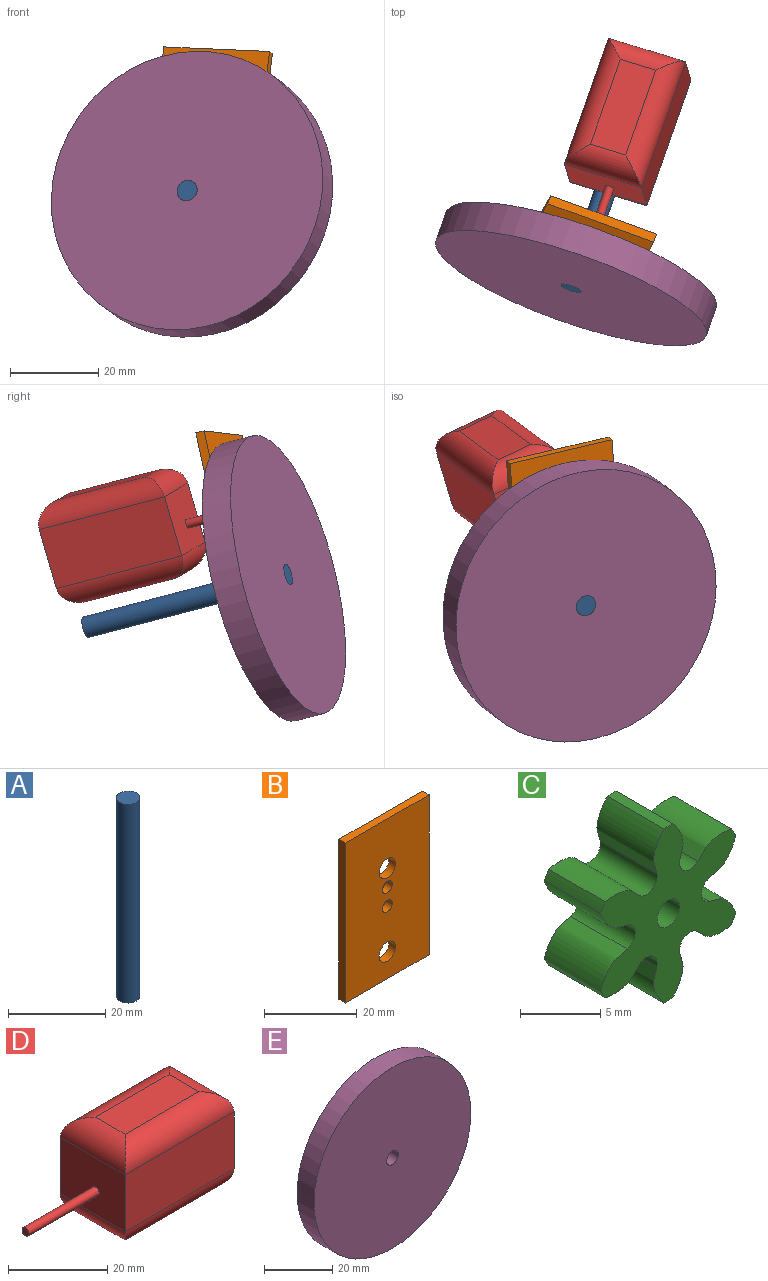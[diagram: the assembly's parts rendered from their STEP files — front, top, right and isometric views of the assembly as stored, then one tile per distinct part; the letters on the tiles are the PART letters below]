
ASSEMBLY  parts=5 mates=4
PART A: 3 faces, bbox 4.8x4.8x50 mm
  f0: cylinder r=2.4mm len=50mm, axis (0,0,-1), area 754mm2, adj f1,f2
  f1: plane 4.8x4.8mm, normal (0,0,1), area 18.1mm2, adj f0
  f2: plane 4.8x4.8mm, normal (0,0,-1), area 18.1mm2, adj f0
PART B: 10 faces, bbox 25.5x2x42.2 mm
  f0: plane 25.5x2mm, normal (0,0,1), area 51mm2, adj f1,f7,f8,f9
  f1: plane 42.2x2mm, normal (-1,0,0), area 84.4mm2, adj f0,f2,f8,f9
  f2: plane 25.5x2mm, normal (0,0,-1), area 51mm2, adj f1,f7,f8,f9
  f3: cylinder r=2.5mm len=5mm, axis (0,1,0), area 31.4mm2, adj f8,f9
  f4: cylinder r=1.5mm len=3mm, axis (0,1,0), area 18.8mm2, adj f8,f9
  f5: cylinder r=1.5mm len=3mm, axis (0,1,0), area 18.8mm2, adj f8,f9
  f6: cylinder r=2.5mm len=5mm, axis (0,1,0), area 31.4mm2, adj f8,f9
  f7: plane 42.2x2mm, normal (1,0,0), area 84.4mm2, adj f0,f2,f8,f9
  f8: plane 42.2x25.5mm, normal (0,-1,0), area 1022.7mm2, adj f0,f1,f2,f3,f4,f5,f6,f7
  f9: plane 42.2x25.5mm, normal (0,1,0), area 1022.7mm2, adj f0,f1,f2,f3,f4,f5,f6,f7
PART C: 27 faces, bbox 12x5x13.4 mm
  f0: cylinder r=6.67mm len=5mm, axis (0,1,0), area 3.9mm2, adj f5,f6,f18,f25
  f1: cylinder r=6.67mm len=5mm, axis (0,1,0), area 3.9mm2, adj f5,f6,f22,f24
  f2: cylinder r=6.67mm len=5mm, axis (0,1,0), area 3.9mm2, adj f5,f6,f15,f19
  f3: cylinder r=6.67mm len=5mm, axis (0,1,0), area 3.9mm2, adj f5,f6,f9,f16
  f4: cylinder r=6.67mm len=5mm, axis (0,1,0), area 3.9mm2, adj f5,f6,f13,f21
  f5: plane 13.39x11.99mm, normal (0,-1,0), area 71.7mm2, adj f0,f1,f2,f3,f4,f7,f8,f9
  f6: plane 13.39x11.99mm, normal (0,1,0), area 71.7mm2, adj f0,f1,f2,f3,f4,f7,f8,f9
  f7: cylinder r=1mm len=5mm, axis (0,1,0), area 31.4mm2, adj f5,f6
  f8: cylinder r=6.67mm len=5mm, axis (0,1,0), area 3.9mm2, adj f5,f6,f10,f12
  f9: extruded ~5x2.33mm, area 16.8mm2, adj f3,f5,f6,f11
  f10: extruded ~5x2.33mm, area 16.8mm2, adj f5,f6,f8,f11
  f11: cylinder r=0.94mm len=5mm, axis (0,1,0), area 12.5mm2, adj f5,f6,f9,f10
  f12: extruded ~5x2.96mm, area 16.8mm2, adj f5,f6,f8,f14
  f13: extruded ~5x3.06mm, area 16.8mm2, adj f4,f5,f6,f14
  f14: cylinder r=0.94mm len=5mm, axis (0,1,0), area 12.5mm2, adj f5,f6,f12,f13
  f15: extruded ~5x3.06mm, area 16.8mm2, adj f2,f5,f6,f17
  f16: extruded ~5x2.96mm, area 16.8mm2, adj f3,f5,f6,f17
  f17: cylinder r=0.94mm len=5mm, axis (0,1,0), area 12.5mm2, adj f5,f6,f15,f16
  f18: extruded ~5x2.96mm, area 16.8mm2, adj f0,f5,f6,f20
  f19: extruded ~5x3.06mm, area 16.8mm2, adj f2,f5,f6,f20
  f20: cylinder r=0.94mm len=5mm, axis (0,1,0), area 12.5mm2, adj f5,f6,f18,f19
  f21: extruded ~5x3.06mm, area 16.8mm2, adj f4,f5,f6,f23
  f22: extruded ~5x2.96mm, area 16.8mm2, adj f1,f5,f6,f23
  f23: cylinder r=0.94mm len=5mm, axis (0,1,0), area 12.5mm2, adj f5,f6,f21,f22
  f24: extruded ~5x2.33mm, area 16.8mm2, adj f1,f5,f6,f26
  f25: extruded ~5x2.33mm, area 16.8mm2, adj f0,f5,f6,f26
  f26: cylinder r=0.94mm len=5mm, axis (0,1,0), area 12.5mm2, adj f5,f6,f24,f25
PART D: 16 faces, bbox 51x18.5x24 mm
  f0: plane 18.5x14mm, normal (-1,0,0), area 255.9mm2, adj f4,f5,f9,f10,f14
  f1: plane 21x8.5mm, normal (0,0,-1), area 178.5mm2, adj f6,f7,f8,f9
  f2: plane 18.5x14mm, normal (1,0,0), area 259mm2, adj f4,f5,f6,f13
  f3: plane 21x8.5mm, normal (0,0,1), area 178.5mm2, adj f10,f11,f12,f13
  f4: plane 31x14mm, normal (0,-1,0), area 434mm2, adj f0,f2,f7,f11
  f5: plane 31x14mm, normal (0,1,0), area 434mm2, adj f0,f2,f8,f12
  f6: cylinder r=5mm len=18.5mm, axis (0,1,0), area 116.8mm2, adj f1,f2,f7,f8
  f7: cylinder r=5mm len=31mm, axis (-1,0,0), area 214.9mm2, adj f1,f4,f6,f9
  f8: cylinder r=5mm len=31mm, axis (1,0,0), area 214.9mm2, adj f1,f5,f6,f9
  f9: cylinder r=5mm len=18.5mm, axis (0,-1,0), area 116.8mm2, adj f0,f1,f7,f8
  f10: cylinder r=5mm len=18.5mm, axis (0,1,0), area 116.8mm2, adj f0,f3,f11,f12
  f11: cylinder r=5mm len=31mm, axis (1,0,0), area 214.9mm2, adj f3,f4,f10,f13
  f12: cylinder r=5mm len=31mm, axis (-1,0,0), area 214.9mm2, adj f3,f5,f10,f13
  f13: cylinder r=5mm len=18.5mm, axis (0,-1,0), area 116.8mm2, adj f2,f3,f11,f12
  f14: cylinder r=1mm len=20mm, axis (1,0,0), area 125.7mm2, adj f0,f15
  f15: plane 2x2mm, normal (-1,0,0), area 3.1mm2, adj f14
PART E: 119 faces, bbox 65x7x65 mm
  f0: cylinder r=2.4mm len=7mm, axis (0,1,0), area 105.6mm2, adj f2,f118
  f1: cylinder r=32.5mm len=65mm, axis (0,1,0), area 1429.4mm2, adj f2,f3
  f2: plane 65x65mm, normal (0,-1,0), area 3300.2mm2, adj f0,f1
  f3: plane 65x65mm, normal (0,1,0), area 1623.9mm2, adj f1,f4,f5,f6,f7,f8,f9,f10
  f4: cylinder r=25mm len=5mm, axis (0,1,0), area 6.1mm2, adj f3,f31,f33,f115
  f5: cylinder r=25mm len=5mm, axis (0,1,0), area 6.1mm2, adj f3,f31,f112,f114
  f6: cylinder r=25mm len=5mm, axis (0,1,0), area 6.1mm2, adj f3,f31,f105,f109
  f7: cylinder r=25mm len=5mm, axis (0,1,0), area 6.1mm2, adj f3,f31,f106,f111
  f8: cylinder r=25mm len=5mm, axis (0,1,0), area 6.1mm2, adj f3,f31,f103,f108
  f9: cylinder r=25mm len=5mm, axis (0,1,0), area 6.1mm2, adj f3,f31,f100,f102
  f10: cylinder r=25mm len=5mm, axis (0,1,0), area 6.1mm2, adj f3,f31,f97,f99
  f11: cylinder r=25mm len=5mm, axis (0,1,0), area 6.1mm2, adj f3,f31,f94,f96
  f12: cylinder r=25mm len=5mm, axis (0,1,0), area 6.1mm2, adj f3,f31,f87,f91
  f13: cylinder r=25mm len=5mm, axis (0,1,0), area 6.1mm2, adj f3,f31,f84,f88
  f14: cylinder r=25mm len=5mm, axis (0,1,0), area 6.1mm2, adj f3,f31,f81,f85
  f15: cylinder r=25mm len=5mm, axis (0,1,0), area 6.1mm2, adj f3,f31,f82,f93
  f16: cylinder r=25mm len=5mm, axis (0,1,0), area 6.1mm2, adj f3,f31,f79,f90
  f17: cylinder r=25mm len=5mm, axis (0,1,0), area 6.1mm2, adj f3,f31,f76,f78
  f18: cylinder r=25mm len=5mm, axis (0,1,0), area 6.1mm2, adj f3,f31,f73,f75
  f19: cylinder r=25mm len=5mm, axis (0,1,0), area 6.1mm2, adj f3,f31,f70,f72
  f20: cylinder r=25mm len=5mm, axis (0,1,0), area 6.1mm2, adj f3,f31,f63,f67
  f21: cylinder r=25mm len=5mm, axis (0,1,0), area 6.1mm2, adj f3,f31,f60,f64
  f22: cylinder r=25mm len=5mm, axis (0,1,0), area 6.1mm2, adj f3,f31,f57,f61
  f23: cylinder r=25mm len=5mm, axis (0,1,0), area 6.1mm2, adj f3,f31,f54,f58
  f24: cylinder r=25mm len=5mm, axis (0,1,0), area 6.1mm2, adj f3,f31,f51,f55
  f25: cylinder r=25mm len=5mm, axis (0,1,0), area 6.1mm2, adj f3,f31,f48,f52
  f26: cylinder r=25mm len=5mm, axis (0,1,0), area 6.1mm2, adj f3,f31,f45,f49
  f27: cylinder r=25mm len=5mm, axis (0,1,0), area 6.1mm2, adj f3,f31,f42,f46
  f28: cylinder r=25mm len=5mm, axis (0,1,0), area 6.1mm2, adj f3,f31,f36,f43
  f29: cylinder r=25mm len=5mm, axis (0,1,0), area 6.1mm2, adj f3,f31,f40,f69
  f30: cylinder r=25mm len=5mm, axis (0,1,0), area 6.1mm2, adj f3,f31,f37,f39
  f31: plane 49.82x49.82mm, normal (0,1,0), area 1630.8mm2, adj f4,f5,f6,f7,f8,f9,f10,f11
  f32: cylinder r=25mm len=5mm, axis (0,1,0), area 6.1mm2, adj f3,f31,f34,f66
  f33: extruded ~5x2.87mm, area 15.8mm2, adj f3,f4,f31,f35
  f34: extruded ~5x2.87mm, area 15.8mm2, adj f3,f31,f32,f35
  f35: cylinder r=0.93mm len=5mm, axis (0,1,0), area 13.1mm2, adj f3,f31,f33,f34
  f36: extruded ~5x3.04mm, area 15.8mm2, adj f3,f28,f31,f38
  f37: extruded ~5x2.79mm, area 15.8mm2, adj f3,f30,f31,f38
  f38: cylinder r=0.93mm len=5mm, axis (0,1,0), area 13.1mm2, adj f3,f31,f36,f37
  f39: extruded ~5x2.79mm, area 15.8mm2, adj f3,f30,f31,f41
  f40: extruded ~5x3.04mm, area 15.8mm2, adj f3,f29,f31,f41
  f41: cylinder r=0.93mm len=5mm, axis (0,1,0), area 13.1mm2, adj f3,f31,f39,f40
  f42: extruded ~5x3.14mm, area 15.8mm2, adj f3,f27,f31,f44
  f43: extruded ~5x2.4mm, area 15.8mm2, adj f3,f28,f31,f44
  f44: cylinder r=0.93mm len=5mm, axis (0,1,0), area 13.1mm2, adj f3,f31,f42,f43
  f45: extruded ~5x3.08mm, area 15.8mm2, adj f3,f26,f31,f47
  f46: extruded ~5x2.52mm, area 15.8mm2, adj f3,f27,f31,f47
  f47: cylinder r=0.93mm len=5mm, axis (0,1,0), area 13.1mm2, adj f3,f31,f45,f46
  f48: extruded ~5x2.87mm, area 15.8mm2, adj f3,f25,f31,f50
  f49: extruded ~5x2.87mm, area 15.8mm2, adj f3,f26,f31,f50
  f50: cylinder r=0.93mm len=5mm, axis (0,1,0), area 13.1mm2, adj f3,f31,f48,f49
  f51: extruded ~5x2.52mm, area 15.8mm2, adj f3,f24,f31,f53
  f52: extruded ~5x3.08mm, area 15.8mm2, adj f3,f25,f31,f53
  f53: cylinder r=0.93mm len=5mm, axis (0,1,0), area 13.1mm2, adj f3,f31,f51,f52
  f54: extruded ~5x2.4mm, area 15.8mm2, adj f3,f23,f31,f56
  f55: extruded ~5x3.14mm, area 15.8mm2, adj f3,f24,f31,f56
  f56: cylinder r=0.93mm len=5mm, axis (0,1,0), area 13.1mm2, adj f3,f31,f54,f55
  f57: extruded ~5x2.79mm, area 15.8mm2, adj f3,f22,f31,f59
  f58: extruded ~5x3.04mm, area 15.8mm2, adj f3,f23,f31,f59
  f59: cylinder r=0.93mm len=5mm, axis (0,1,0), area 13.1mm2, adj f3,f31,f57,f58
  f60: extruded ~5x3.04mm, area 15.8mm2, adj f3,f21,f31,f62
  f61: extruded ~5x2.79mm, area 15.8mm2, adj f3,f22,f31,f62
  f62: cylinder r=0.93mm len=5mm, axis (0,1,0), area 13.1mm2, adj f3,f31,f60,f61
  f63: extruded ~5x3.14mm, area 15.8mm2, adj f3,f20,f31,f65
  f64: extruded ~5x2.4mm, area 15.8mm2, adj f3,f21,f31,f65
  f65: cylinder r=0.93mm len=5mm, axis (0,1,0), area 13.1mm2, adj f3,f31,f63,f64
  f66: extruded ~5x3.08mm, area 15.8mm2, adj f3,f31,f32,f68
  f67: extruded ~5x2.52mm, area 15.8mm2, adj f3,f20,f31,f68
  f68: cylinder r=0.93mm len=5mm, axis (0,1,0), area 13.1mm2, adj f3,f31,f66,f67
  f69: extruded ~5x2.4mm, area 15.8mm2, adj f3,f29,f31,f71
  f70: extruded ~5x3.14mm, area 15.8mm2, adj f3,f19,f31,f71
  f71: cylinder r=0.93mm len=5mm, axis (0,1,0), area 13.1mm2, adj f3,f31,f69,f70
  f72: extruded ~5x2.52mm, area 15.8mm2, adj f3,f19,f31,f74
  f73: extruded ~5x3.08mm, area 15.8mm2, adj f3,f18,f31,f74
  f74: cylinder r=0.93mm len=5mm, axis (0,1,0), area 13.1mm2, adj f3,f31,f72,f73
  f75: extruded ~5x2.87mm, area 15.8mm2, adj f3,f18,f31,f77
  f76: extruded ~5x2.87mm, area 15.8mm2, adj f3,f17,f31,f77
  f77: cylinder r=0.93mm len=5mm, axis (0,1,0), area 13.1mm2, adj f3,f31,f75,f76
  f78: extruded ~5x3.08mm, area 15.8mm2, adj f3,f17,f31,f80
  f79: extruded ~5x2.52mm, area 15.8mm2, adj f3,f16,f31,f80
  f80: cylinder r=0.93mm len=5mm, axis (0,1,0), area 13.1mm2, adj f3,f31,f78,f79
  f81: extruded ~5x2.4mm, area 15.8mm2, adj f3,f14,f31,f83
  f82: extruded ~5x3.14mm, area 15.8mm2, adj f3,f15,f31,f83
  f83: cylinder r=0.93mm len=5mm, axis (0,1,0), area 13.1mm2, adj f3,f31,f81,f82
  f84: extruded ~5x2.79mm, area 15.8mm2, adj f3,f13,f31,f86
  f85: extruded ~5x3.04mm, area 15.8mm2, adj f3,f14,f31,f86
  f86: cylinder r=0.93mm len=5mm, axis (0,1,0), area 13.1mm2, adj f3,f31,f84,f85
  f87: extruded ~5x3.04mm, area 15.8mm2, adj f3,f12,f31,f89
  f88: extruded ~5x2.79mm, area 15.8mm2, adj f3,f13,f31,f89
  f89: cylinder r=0.93mm len=5mm, axis (0,1,0), area 13.1mm2, adj f3,f31,f87,f88
  f90: extruded ~5x3.14mm, area 15.8mm2, adj f3,f16,f31,f92
  f91: extruded ~5x2.4mm, area 15.8mm2, adj f3,f12,f31,f92
  f92: cylinder r=0.93mm len=5mm, axis (0,1,0), area 13.1mm2, adj f3,f31,f90,f91
  f93: extruded ~5x2.52mm, area 15.8mm2, adj f3,f15,f31,f95
  f94: extruded ~5x3.08mm, area 15.8mm2, adj f3,f11,f31,f95
  f95: cylinder r=0.93mm len=5mm, axis (0,1,0), area 13.1mm2, adj f3,f31,f93,f94
  f96: extruded ~5x2.87mm, area 15.8mm2, adj f3,f11,f31,f98
  f97: extruded ~5x2.87mm, area 15.8mm2, adj f3,f10,f31,f98
  f98: cylinder r=0.93mm len=5mm, axis (0,1,0), area 13.1mm2, adj f3,f31,f96,f97
  f99: extruded ~5x3.08mm, area 15.8mm2, adj f3,f10,f31,f101
  f100: extruded ~5x2.52mm, area 15.8mm2, adj f3,f9,f31,f101
  f101: cylinder r=0.93mm len=5mm, axis (0,1,0), area 13.1mm2, adj f3,f31,f99,f100
  f102: extruded ~5x3.14mm, area 15.8mm2, adj f3,f9,f31,f104
  f103: extruded ~5x2.4mm, area 15.8mm2, adj f3,f8,f31,f104
  f104: cylinder r=0.93mm len=5mm, axis (0,1,0), area 13.1mm2, adj f3,f31,f102,f103
  f105: extruded ~5x2.79mm, area 15.8mm2, adj f3,f6,f31,f107
  f106: extruded ~5x3.04mm, area 15.8mm2, adj f3,f7,f31,f107
  f107: cylinder r=0.93mm len=5mm, axis (0,1,0), area 13.1mm2, adj f3,f31,f105,f106
  f108: extruded ~5x3.04mm, area 15.8mm2, adj f3,f8,f31,f110
  f109: extruded ~5x2.79mm, area 15.8mm2, adj f3,f6,f31,f110
  f110: cylinder r=0.93mm len=5mm, axis (0,1,0), area 13.1mm2, adj f3,f31,f108,f109
  f111: extruded ~5x2.4mm, area 15.8mm2, adj f3,f7,f31,f113
  f112: extruded ~5x3.14mm, area 15.8mm2, adj f3,f5,f31,f113
  f113: cylinder r=0.93mm len=5mm, axis (0,1,0), area 13.1mm2, adj f3,f31,f111,f112
  f114: extruded ~5x2.52mm, area 15.8mm2, adj f3,f5,f31,f116
  f115: extruded ~5x3.08mm, area 15.8mm2, adj f3,f4,f31,f116
  f116: cylinder r=0.93mm len=5mm, axis (0,1,0), area 13.1mm2, adj f3,f31,f114,f115
  f117: cylinder r=4.5mm len=9mm, axis (0,-1,0), area 141.4mm2, adj f31,f118
  f118: plane 9x9mm, normal (0,1,0), area 45.5mm2, adj f0,f117
PLACE A rot(axis=(0.96,-0.14,-0.23),78.8deg) t=(-6.41,135.28,-47.1)mm
PLACE B rot(axis=(-0.55,0.19,-0.81),24.1deg) t=(25.24,100.17,7.57)mm fixed
PLACE C rot(axis=(-0.74,0.2,0.64),178.1deg) t=(14.68,68.02,33.36)mm
PLACE D rot(axis=(-0.23,0.08,0.97),73.6deg) t=(19.5,106.1,11.38)mm
PLACE E rot(axis=(-0.58,-0.58,-0.58),29.1deg) t=(14.6,69.93,15.44)mm
MATE revolute B.f3 <-> A.f0  axis (0.32,0.92,-0.24) through (14.92,70.85,15.2)mm
MATE revolute B.f4 <-> D.f14  axis (0.32,0.92,-0.24) through (17.25,75.35,31.46)mm
MATE revolute E.f0 <-> A.f0  axis (-0.32,-0.92,0.24) through (12.34,63.52,17.11)mm
MATE revolute C.f0 <-> D.f14  axis (-0.32,-0.92,0.24) through (14.68,68.02,33.36)mm
